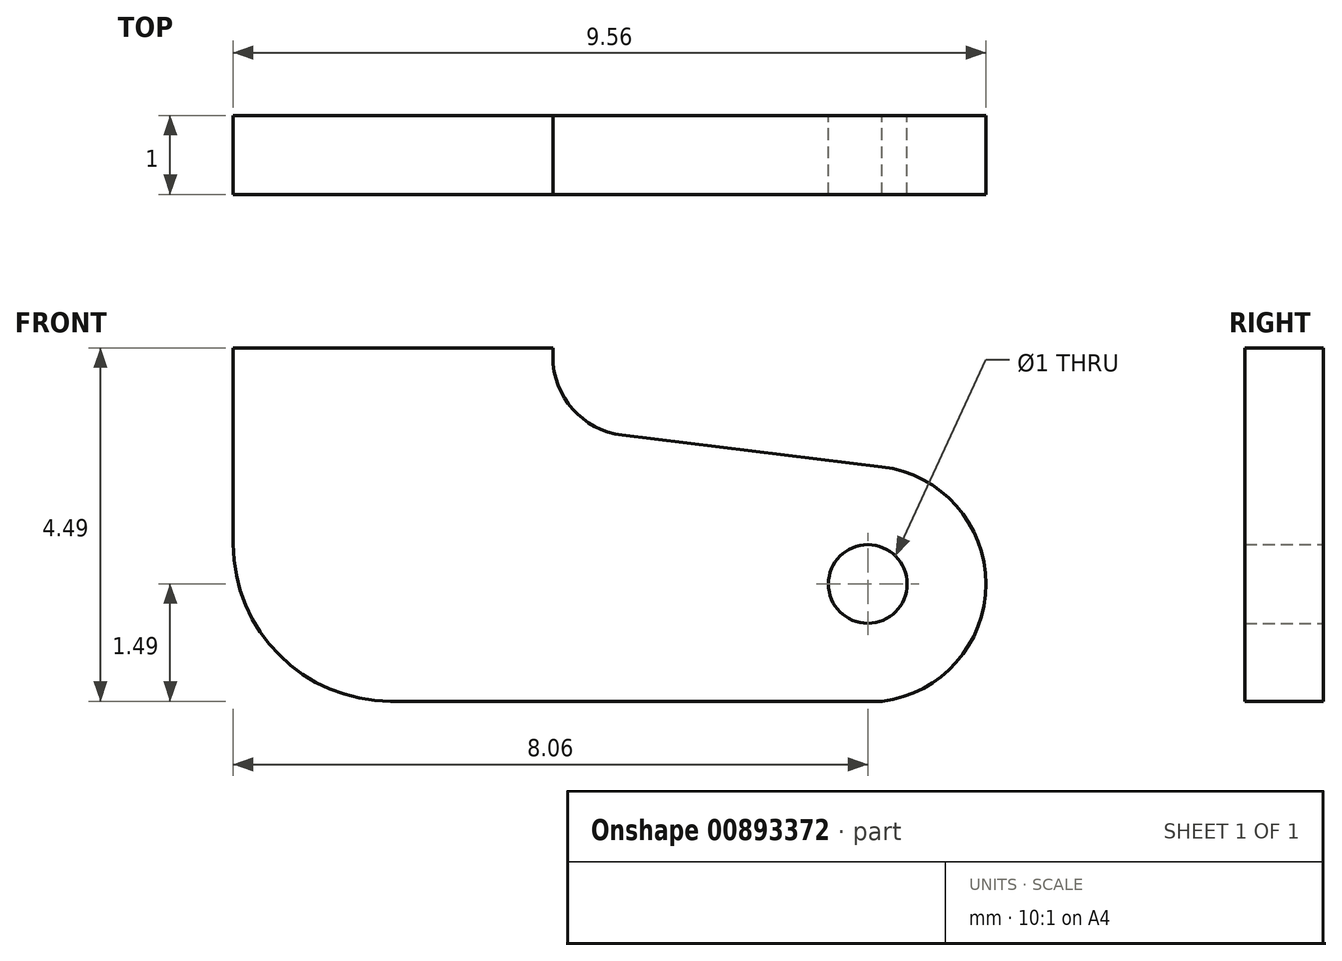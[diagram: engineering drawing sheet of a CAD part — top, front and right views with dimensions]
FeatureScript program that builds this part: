
annotation { "Feature Type Name" : "Feature", "Feature Type Description" : "" }
export const myFeature = defineFeature(function(context is Context, id is Id, definition is map)
    precondition{}
    {
        {
            var Q0;
            Q0=qCreatedBy(makeId("Front.planeOp"),FACE);
            var sketch = newSketch(context, id + "F0", { "sketchPlane" : qUnion([Q0])});
            skArc(sketch, "E0", {"start": v(0.18, -1.49) * mm, "mid": v(1.5, 0) * mm, "end": v(0.18, 1.49) * mm});
            skPoint(sketch, "E1.start.orphan", {"position": v(-16.68, 0) * mm});
            skLineSegment(sketch, "E2", {"start": v(-3.12, 1.9) * mm, "end": v(0.18, 1.49) * mm});
            skLineSegment(sketch, "E3", {"start": v(0.18, -1.49) * mm, "end": v(-6.06, -1.49) * mm});
            skLineSegment(sketch, "E4", {"start": v(-8.06, 0.51) * mm, "end": v(-8.06, 3) * mm});
            skLineSegment(sketch, "E5", {"start": v(-8.06, 3) * mm, "end": v(-4, 3) * mm});
            skLineSegment(sketch, "E6", {"start": v(-4, 2.89) * mm, "end": v(-4, 3) * mm});
            skPoint(sketch, "E7.visualSharp", {"position": v(-8.06, -1.49) * mm});
            skArc(sketch, "E7.filletArc", {"start": v(-8.06, 0.51) * mm, "mid": v(-7.47, -0.9) * mm, "end": v(-6.06, -1.49) * mm});
            skPoint(sketch, "E8.visualSharp", {"position": v(-4, 2) * mm});
            skArc(sketch, "E8.filletArc", {"start": v(-4, 2.89) * mm, "mid": v(-3.75, 2.22) * mm, "end": v(-3.12, 1.9) * mm});
            skCircle(sketch, "E9", {"center": v(0, 0) * mm, "radius": 0.5 * mm});
            skSolve(sketch);
        }
        {
            var Q0;
            Q0 = qSketchRegion(id + "F0", true);
            extrude(context, id + "F1", {"entities" : qUnion([Q0]), "depth" : 1 * mm, "offsetDistance" : 25 * mm});
        }
    });
